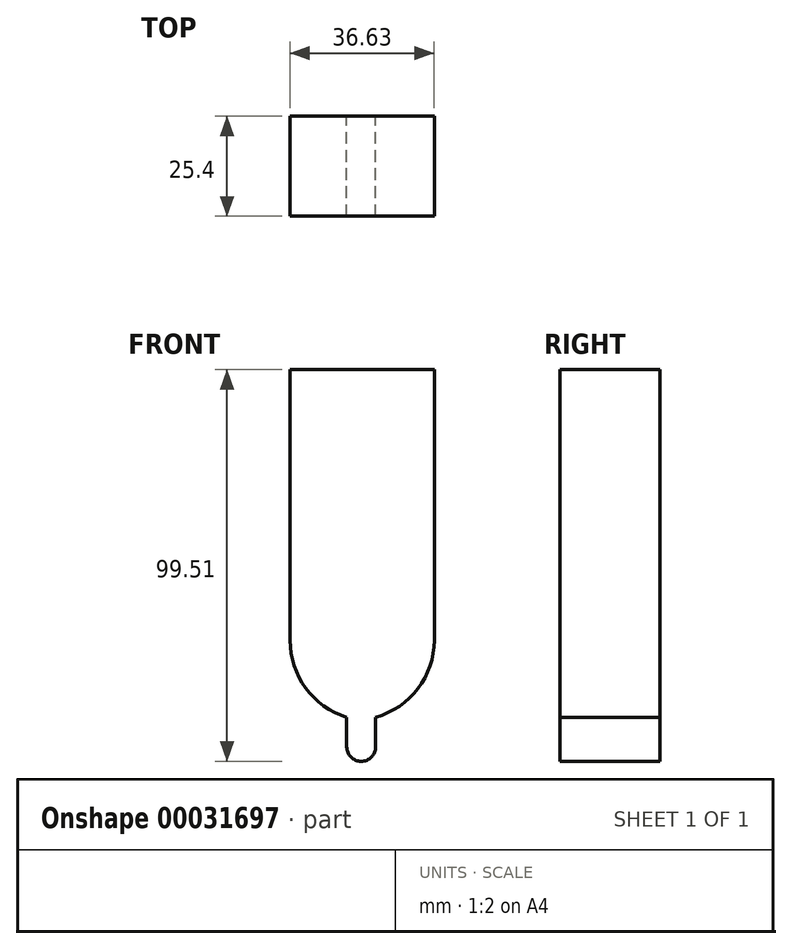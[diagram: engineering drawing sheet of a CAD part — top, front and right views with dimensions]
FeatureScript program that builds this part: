
annotation { "Feature Type Name" : "Feature", "Feature Type Description" : "" }
export const myFeature = defineFeature(function(context is Context, id is Id, definition is map)
    precondition{}
    {
        {
            var Q0;
            Q0=qCreatedBy(makeId("Front.planeOp"),FACE);
            var sketch = newSketch(context, id + "F0", { "sketchPlane" : qUnion([Q0])});
            skLineSegment(sketch, "E0", {"start": v(-21.76, 68.74) * mm, "end": v(-21.76, 0) * mm});
            skLineSegment(sketch, "E1", {"start": v(14.87, 0) * mm, "end": v(14.87, 68.74) * mm});
            skArc(sketch, "E2", {"start": v(-21.76, 0) * mm, "mid": v(-17.77, -12.15) * mm, "end": v(-7.36, -19.57) * mm});
            skArc(sketch, "E3", {"start": v(0, -19.57) * mm, "mid": v(10.73, -12.3) * mm, "end": v(14.87, 0) * mm});
            skLineSegment(sketch, "E4", {"start": v(-21.76, 68.74) * mm, "end": v(14.87, 68.74) * mm});
            skLineSegment(sketch, "E5", {"start": v(-21.76, 50.89) * mm, "end": v(14.87, 50.89) * mm});
            skLineSegment(sketch, "E6", {"start": v(-21.76, 28.97) * mm, "end": v(14.87, 28.97) * mm});
            skLineSegment(sketch, "E7", {"start": v(14.87, 8.3) * mm, "end": v(-21.76, 8.3) * mm});
            skLineSegment(sketch, "E8", {"start": v(-7.36, -19.57) * mm, "end": v(-7.36, -27.09) * mm});
            skLineSegment(sketch, "E9", {"start": v(-7.36, -27.09) * mm, "end": v(0, -27.09) * mm});
            skLineSegment(sketch, "E10", {"start": v(0, -27.09) * mm, "end": v(0, -19.57) * mm});
            skArc(sketch, "E11", {"start": v(-7.36, -27.09) * mm, "mid": v(-3.68, -30.77) * mm, "end": v(0, -27.09) * mm});
            skSolve(sketch);
        }
        {
            var Q0;
            Q0 = qSketchRegion(id + "F0", true);
            extrude(context, id + "F1", {"entities" : qUnion([Q0]), "depth" : 25.4 * mm});
        }
    });
